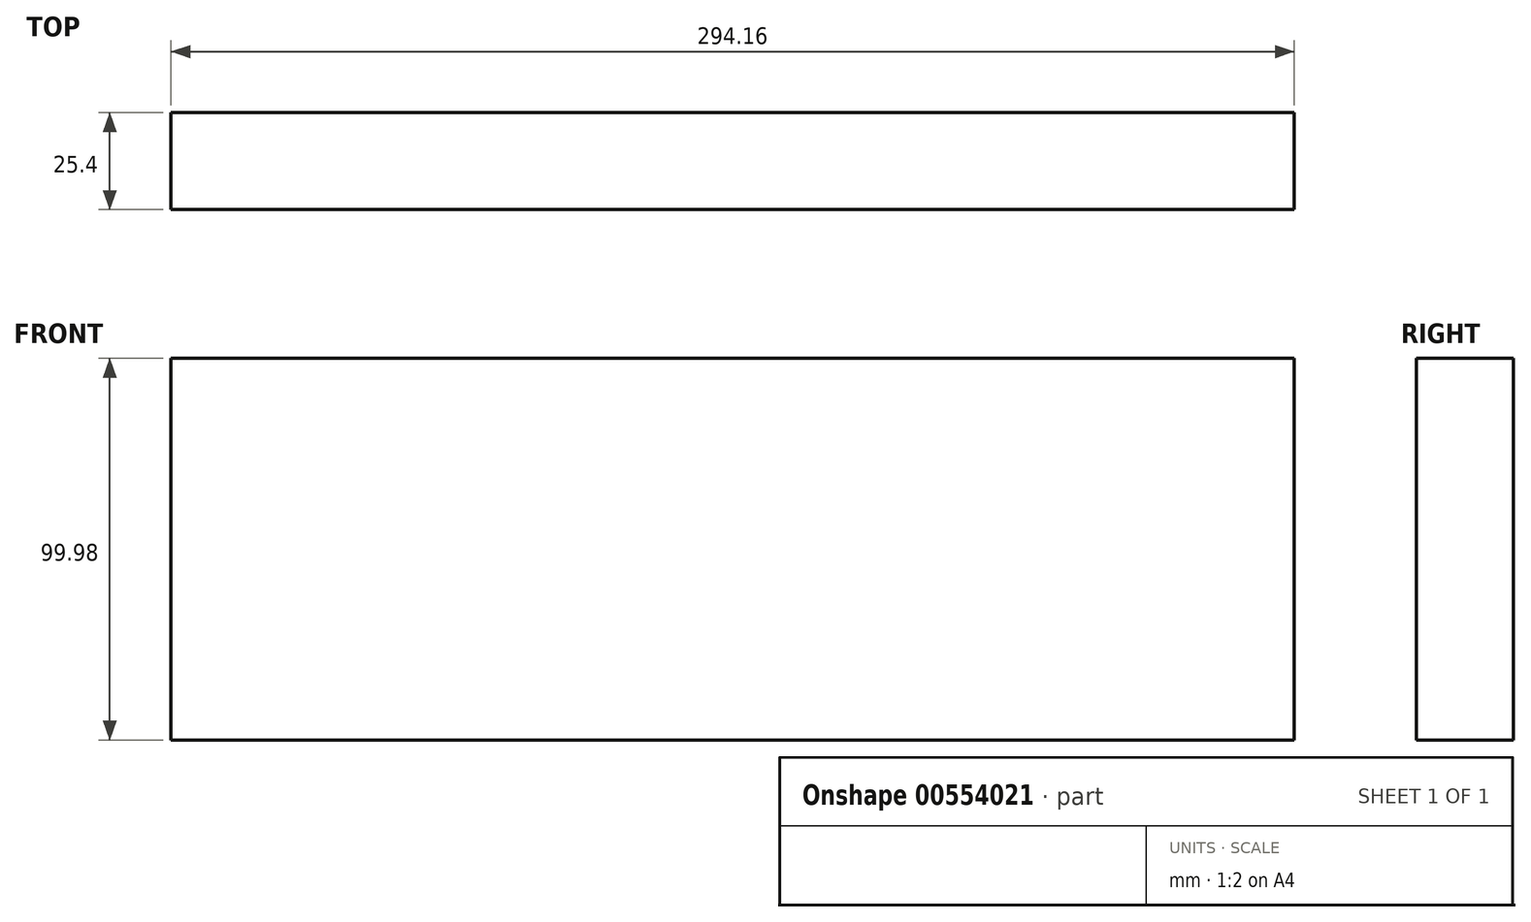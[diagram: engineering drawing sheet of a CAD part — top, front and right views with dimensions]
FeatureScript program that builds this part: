
annotation { "Feature Type Name" : "Feature", "Feature Type Description" : "" }
export const myFeature = defineFeature(function(context is Context, id is Id, definition is map)
    precondition{}
    {
        {
            var Q0;
            Q0=qCreatedBy(makeId("Front.planeOp"),FACE);
            var sketch = newSketch(context, id + "F0", { "sketchPlane" : qUnion([Q0])});
            skLineSegment(sketch, "E0.bottom", {"start": v(-73.1, 49.99) * mm, "end": v(221.06, 49.99) * mm});
            skLineSegment(sketch, "E0.top", {"start": v(-73.1, -49.99) * mm, "end": v(221.06, -49.99) * mm});
            skLineSegment(sketch, "E0.left", {"start": v(-73.1, 49.99) * mm, "end": v(-73.1, -49.99) * mm});
            skLineSegment(sketch, "E0.right", {"start": v(221.06, 49.99) * mm, "end": v(221.06, -49.99) * mm});
            skPoint(sketch, "E0.middle", {"position": v(73.98, 0) * mm});
            skSolve(sketch);
        }
        {
            var Q0;
            Q0=makeQuery(id+"F0.imprint","IMPRINT",FACE,{"disambiguationData":[TD([[makeQuery(id+"F0.imprint","IMPRINT",EDGE,{"derivedFrom":sQuery(id+"F0.wireOp",EDGE,"E0.bottom")}),-1.0]])]});
            extrude(context, id + "F1", {"entities" : qUnion([Q0]), "depth" : 25.4 * mm, "offsetDistance" : 25.4 * mm});
        }
    });
